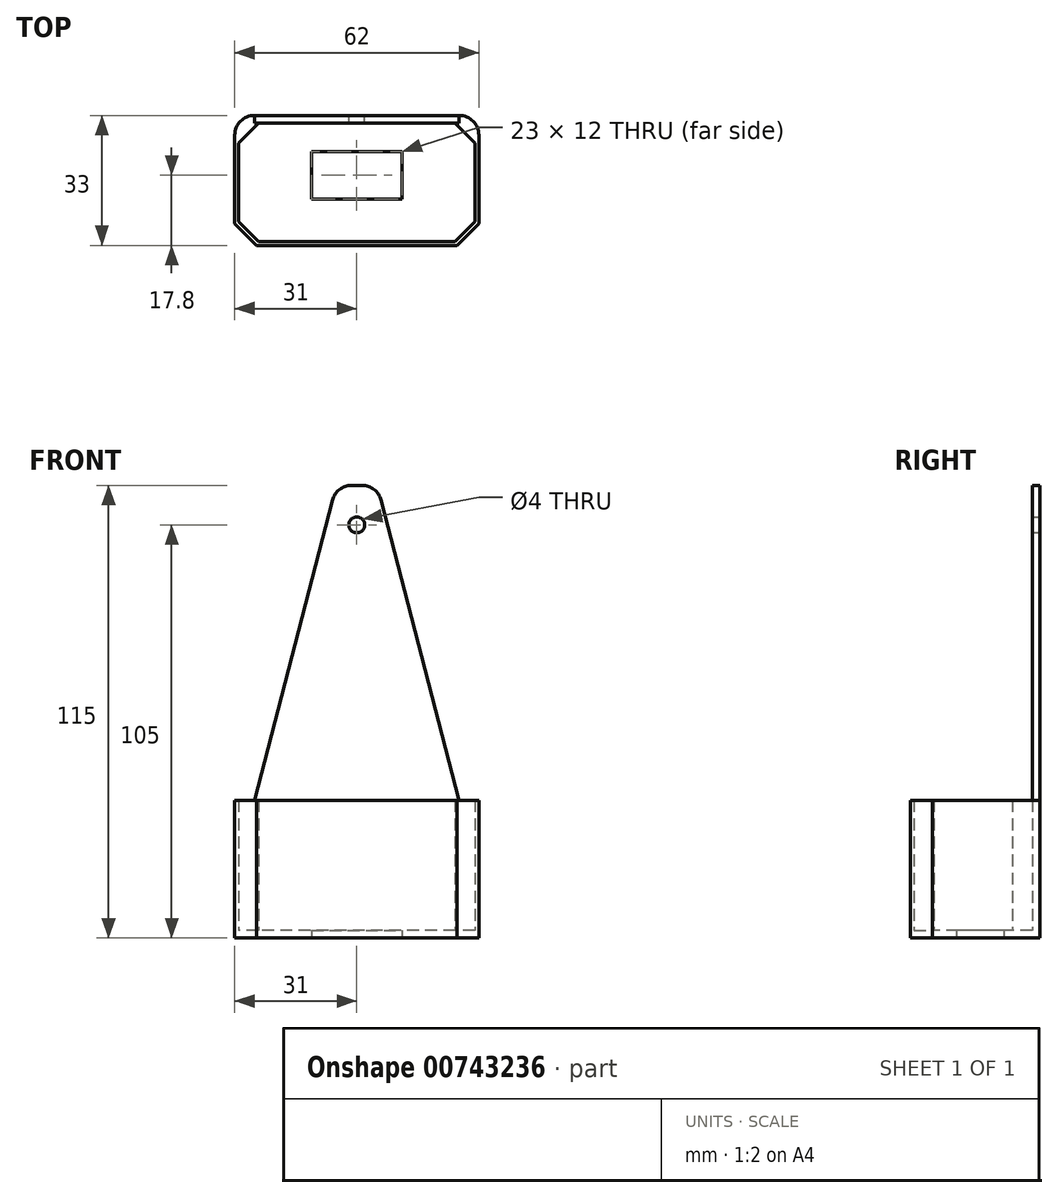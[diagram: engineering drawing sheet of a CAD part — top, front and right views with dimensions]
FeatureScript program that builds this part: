
annotation { "Feature Type Name" : "Feature", "Feature Type Description" : "" }
export const myFeature = defineFeature(function(context is Context, id is Id, definition is map)
    precondition{}
    {
        {
            var Q0;
            Q0=qCreatedBy(makeId("Top.planeOp"),FACE);
            var sketch = newSketch(context, id + "F0", { "sketchPlane" : qUnion([Q0])});
            skLineSegment(sketch, "E0", {"start": v(5, 0) * mm, "end": v(0, 5) * mm});
            skLineSegment(sketch, "E1", {"start": v(0, 5) * mm, "end": v(0, 25) * mm});
            skLineSegment(sketch, "E2", {"start": v(0, 25) * mm, "end": v(5, 30) * mm});
            skLineSegment(sketch, "E3", {"start": v(5, 30) * mm, "end": v(55, 30) * mm});
            skLineSegment(sketch, "E4", {"start": v(55, 30) * mm, "end": v(60, 25) * mm});
            skLineSegment(sketch, "E5", {"start": v(60, 25) * mm, "end": v(60, 5) * mm});
            skLineSegment(sketch, "E6", {"start": v(60, 5) * mm, "end": v(55, 0) * mm});
            skLineSegment(sketch, "E7", {"start": v(55, 0) * mm, "end": v(5, 0) * mm});
            skLineSegment(sketch, "E8.bottom", {"start": v(18.5, 22.8) * mm, "end": v(41.5, 22.8) * mm});
            skLineSegment(sketch, "E8.top", {"start": v(18.5, 10.8) * mm, "end": v(41.5, 10.8) * mm});
            skLineSegment(sketch, "E8.left", {"start": v(18.5, 22.8) * mm, "end": v(18.5, 10.8) * mm});
            skLineSegment(sketch, "E8.right", {"start": v(41.5, 22.8) * mm, "end": v(41.5, 10.8) * mm});
            skSolve(sketch);
        }
        {
            var Q0;
            Q0=makeQuery(id+"F0.imprint","IMPRINT",FACE,{"disambiguationData":[TD([[makeQuery(id+"F0.imprint","IMPRINT",EDGE,{"derivedFrom":sQuery(id+"F0.wireOp",EDGE,"E0")}),-1.0]])]});
            extrude(context, id + "F1", {"entities" : qUnion([Q0]), "depth" : 2 * mm, "offsetDistance" : 25 * mm});
        }
        {
            var Q0;
            Q0=makeQuery(id+"F1.opExtrude","CAP_FACE",FACE,{"disambiguationData":[OSD([sQuery(id+"F0.wireOp",EDGE,"E0"),sQuery(id+"F0.wireOp",EDGE,"E1"),sQuery(id+"F0.wireOp",EDGE,"E2"),sQuery(id+"F0.wireOp",EDGE,"E3"),sQuery(id+"F0.wireOp",EDGE,"E4"),sQuery(id+"F0.wireOp",EDGE,"E5"),sQuery(id+"F0.wireOp",EDGE,"E6"),sQuery(id+"F0.wireOp",EDGE,"E7"),sQuery(id+"F0.wireOp",EDGE,"E8.bottom"),sQuery(id+"F0.wireOp",EDGE,"E8.top"),sQuery(id+"F0.wireOp",EDGE,"E8.left"),sQuery(id+"F0.wireOp",EDGE,"E8.right")])],"isStart":true});
            var sketch = newSketch(context, id + "F2", { "sketchPlane" : qUnion([Q0])});
            skLineSegment(sketch, "E9.0", {"start": v(61, -4.59) * mm, "end": v(55.41, 1) * mm});
            skLineSegment(sketch, "E10.0", {"start": v(61, -27) * mm, "end": v(61, -4.59) * mm});
            skLineSegment(sketch, "E11.0", {"start": v(4, -32) * mm, "end": v(56, -32) * mm});
            skLineSegment(sketch, "E12.0", {"start": v(-1, -4.59) * mm, "end": v(-1, -27) * mm});
            skLineSegment(sketch, "E13.0", {"start": v(4.59, 1) * mm, "end": v(-1, -4.59) * mm});
            skLineSegment(sketch, "E14.0", {"start": v(55.41, 1) * mm, "end": v(4.59, 1) * mm});
            skPoint(sketch, "E15.visualSharp", {"position": v(-1, -32) * mm});
            skArc(sketch, "E15.filletArc", {"start": v(-1, -27) * mm, "mid": v(0.46, -30.54) * mm, "end": v(4, -32) * mm});
            skPoint(sketch, "E16.visualSharp", {"position": v(61, -32) * mm});
            skArc(sketch, "E16.filletArc", {"start": v(56, -32) * mm, "mid": v(59.54, -30.54) * mm, "end": v(61, -27) * mm});
            skLineSegment(sketch, "E17", {"start": v(0, -25) * mm, "end": v(0, -5) * mm});
            skLineSegment(sketch, "E18", {"start": v(0, -5) * mm, "end": v(5, 0) * mm});
            skLineSegment(sketch, "E19", {"start": v(5, 0) * mm, "end": v(55, 0) * mm});
            skLineSegment(sketch, "E20", {"start": v(55, 0) * mm, "end": v(60, -5) * mm});
            skLineSegment(sketch, "E21", {"start": v(60, -5) * mm, "end": v(60, -25) * mm});
            skLineSegment(sketch, "E22", {"start": v(60, -25) * mm, "end": v(55, -30) * mm});
            skLineSegment(sketch, "E23", {"start": v(55, -30) * mm, "end": v(5, -30) * mm});
            skLineSegment(sketch, "E24", {"start": v(5, -30) * mm, "end": v(0, -25) * mm});
            skSolve(sketch);
        }
        {
            var Q0;
            Q0 = qSketchRegion(id + "F2", true);
            extrude(context, id + "F3", {"entities" : qUnion([Q0]), "operationType" : NewBodyOperationType.ADD, "oppositeDirection" : true, "depth" : 35 * mm, "offsetDistance" : 25 * mm});
        }
        {
            var Q0;
            Q0=makeQuery(id+"F3.opExtrude","SWEPT_FACE",FACE,{"disambiguationData":[OSD([sQuery(id+"F2.wireOp",EDGE,"E11.0")])]});
            var sketch = newSketch(context, id + "F4", { "sketchPlane" : qUnion([Q0])});
            skLineSegment(sketch, "E25", {"start": v(-30, 35) * mm, "end": v(-30, 115) * mm});
            skLineSegment(sketch, "E26", {"start": v(-36.17, 111.26) * mm, "end": v(-56, 35) * mm});
            skLineSegment(sketch, "E27", {"start": v(-23.83, 111.26) * mm, "end": v(-4, 35) * mm});
            skCircle(sketch, "E28", {"center": v(-30, 105) * mm, "radius": 2 * mm});
            skLineSegment(sketch, "E29", {"start": v(-31.33, 115) * mm, "end": v(-28.67, 115) * mm});
            skPoint(sketch, "E30.visualSharp", {"position": v(-35.2, 115) * mm});
            skArc(sketch, "E30.filletArc", {"start": v(-31.33, 115) * mm, "mid": v(-34.4, 113.96) * mm, "end": v(-36.17, 111.26) * mm});
            skPoint(sketch, "E31.visualSharp", {"position": v(-24.8, 115) * mm});
            skArc(sketch, "E31.filletArc", {"start": v(-23.83, 111.26) * mm, "mid": v(-25.6, 113.96) * mm, "end": v(-28.67, 115) * mm});
            skSolve(sketch);
        }
        {
            var Q0;
            {var subQ0=sQuery(id+"F4.wireOp",EDGE,"E26");Q0=makeQuery(id+"F4.imprint","IMPRINT",FACE,{"disambiguationData":[TD([[makeQuery(id+"F4.imprint","IMPRINT",EDGE,{"derivedFrom":subQ0}),1.0]])]});}
            var Q1;
            {var subQ4=sQuery(id+"F4.wireOp",EDGE,"E27");Q1=makeQuery(id+"F4.imprint","IMPRINT",FACE,{"disambiguationData":[TD([[makeQuery(id+"F4.imprint","IMPRINT",EDGE,{"derivedFrom":subQ4}),-1.0]])]});}
            extrude(context, id + "F5", {"entities" : qUnion([Q0, Q1]), "operationType" : NewBodyOperationType.ADD, "oppositeDirection" : true, "depth" : 2 * mm, "offsetDistance" : 25 * mm});
        }
    });
